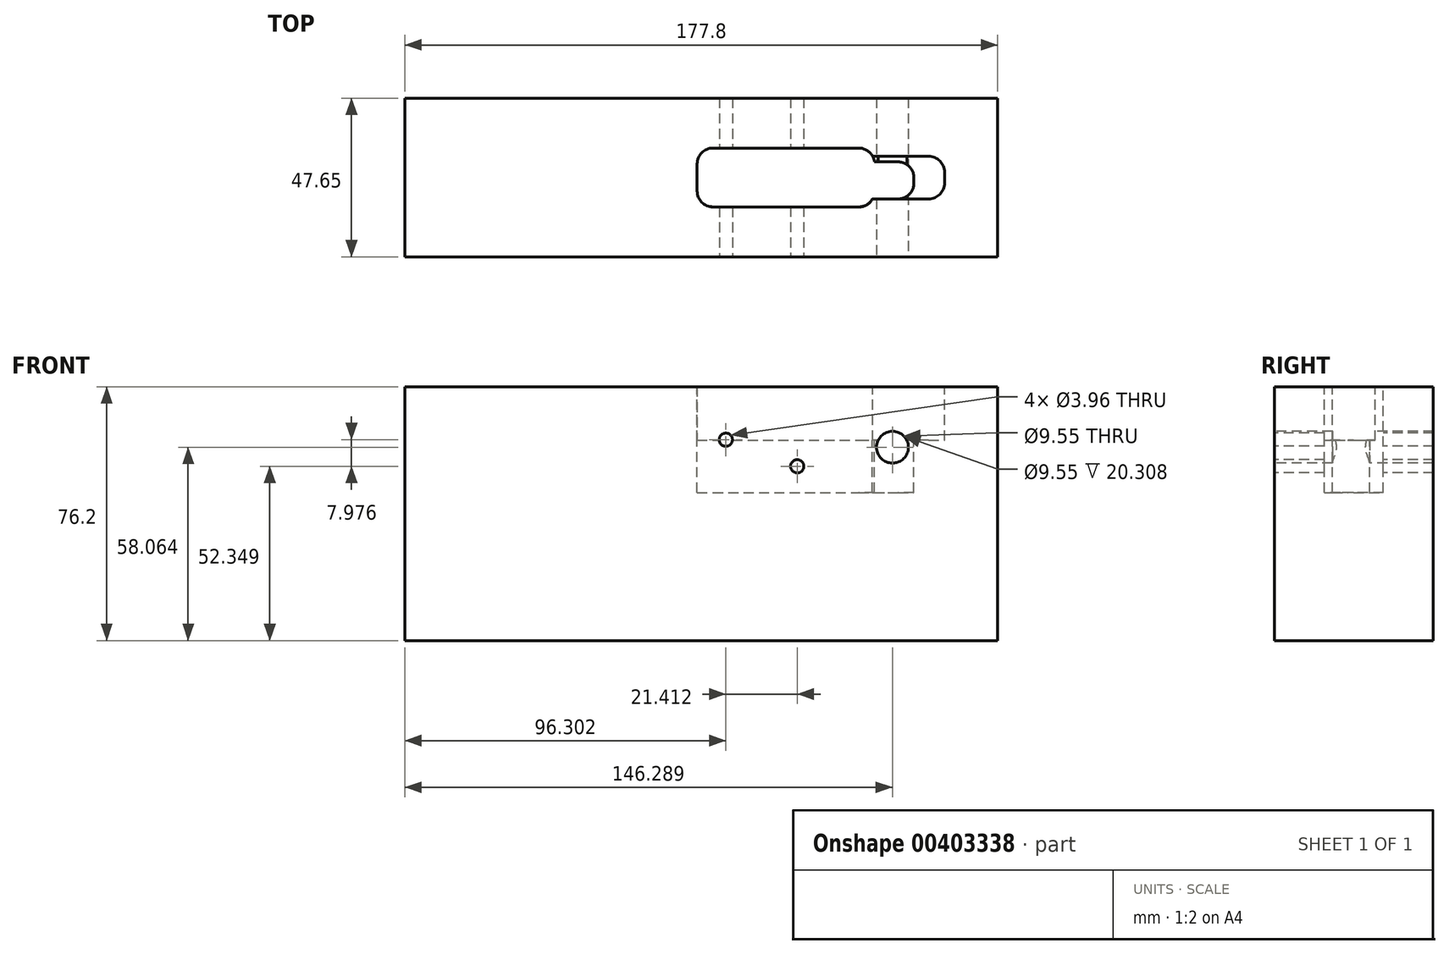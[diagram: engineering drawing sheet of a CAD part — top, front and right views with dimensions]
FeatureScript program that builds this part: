
annotation { "Feature Type Name" : "Feature", "Feature Type Description" : "" }
export const myFeature = defineFeature(function(context is Context, id is Id, definition is map)
    precondition{}
    {
        {
            var Q0;
            Q0=qCreatedBy(makeId("Top.planeOp"),FACE);
            var sketch = newSketch(context, id + "F0", { "sketchPlane" : qUnion([Q0])});
            skLineSegment(sketch, "E0.bottom", {"start": v(-4.76, 47.65) * mm, "end": v(173.04, 47.65) * mm});
            skLineSegment(sketch, "E0.top", {"start": v(-4.76, 0) * mm, "end": v(173.04, 0) * mm});
            skLineSegment(sketch, "E0.left", {"start": v(-4.76, 47.65) * mm, "end": v(-4.76, 0) * mm});
            skLineSegment(sketch, "E0.right", {"start": v(173.04, 47.65) * mm, "end": v(173.04, 0) * mm});
            skLineSegment(sketch, "E1", {"start": v(173, 23.83) * mm, "end": v(-20.73, 23.83) * mm, "construction": true});
            skPoint(sketch, "E1.startSnap0", {"position": v(173.04, 23.83) * mm});
            skPoint(sketch, "E1.endSnap0", {"position": v(-4.76, 23.83) * mm});
            skSolve(sketch);
        }
        {
            var Q0;
            Q0=makeQuery(id+"F0.imprint","IMPRINT",FACE,{"disambiguationData":[TD([[makeQuery(id+"F0.imprint","IMPRINT",EDGE,{"derivedFrom":sQuery(id+"F0.wireOp",EDGE,"E0.bottom")}),-1.0]])]});
            extrude(context, id + "F1", {"entities" : qUnion([Q0]), "oppositeDirection" : true, "depth" : 69.85 * mm, "hasSecondDirection" : true, "secondDirectionOppositeDirection" : false, "secondDirectionDepth" : 6.35 * mm});
        }
        {
            var Q0;
            Q0=qCreatedBy(makeId("Front.planeOp"),FACE);
            var sketch = newSketch(context, id + "F2", { "sketchPlane" : qUnion([Q0])});
            skCircle(sketch, "E2", {"center": v(0, 0) * mm, "radius": 3.18 * mm, "construction": true});
            skCircle(sketch, "E3", {"center": v(141.53, -11.79) * mm, "radius": 4.78 * mm});
            skCircle(sketch, "E4", {"center": v(112.95, -17.5) * mm, "radius": 1.98 * mm});
            skCircle(sketch, "E5", {"center": v(91.54, -9.52) * mm, "radius": 1.98 * mm});
            skCircle(sketch, "E6", {"center": v(161.93, 0) * mm, "radius": 3.18 * mm, "construction": true});
            skSolve(sketch);
        }
        {
            var Q0;
            Q0=qSketchRegion(id+"F2",true);
            extrude(context, id + "F3", {"entities" : qUnion([Q0]), "operationType" : NewBodyOperationType.REMOVE, "endBound" : BoundingType.THROUGH_ALL, "oppositeDirection" : true, "depth" : 25.4 * mm});
        }
        {
            var Q0;
            Q0=makeQuery(id+"F1.opExtrude","CAP_FACE",FACE,{"disambiguationData":[OSD([sQuery(id+"F0.wireOp",EDGE,"E0.bottom"),sQuery(id+"F0.wireOp",EDGE,"E0.top"),sQuery(id+"F0.wireOp",EDGE,"E0.left"),sQuery(id+"F0.wireOp",EDGE,"E0.right")])],"isStart":true});
            var sketch = newSketch(context, id + "F4", { "sketchPlane" : qUnion([Q0])});
            skLineSegment(sketch, "E7.right", {"start": v(148.53, 23.06) * mm, "end": v(148.5, 23.05) * mm});
            skPoint(sketch, "E8.visualSharp", {"position": v(135.54, 17.38) * mm});
            skLineSegment(sketch, "E9.bottom", {"start": v(87.7, 32.6) * mm, "end": v(131.4, 32.6) * mm});
            skLineSegment(sketch, "E9.top", {"start": v(87.7, 14.95) * mm, "end": v(131.4, 14.95) * mm});
            skLineSegment(sketch, "E9.left", {"start": v(82.93, 27.84) * mm, "end": v(82.93, 19.72) * mm});
            skArc(sketch, "E10.filletArc", {"start": v(87.7, 32.6) * mm, "mid": v(84.33, 31.21) * mm, "end": v(82.93, 27.84) * mm});
            skArc(sketch, "E11.filletArc", {"start": v(82.93, 19.72) * mm, "mid": v(84.33, 16.35) * mm, "end": v(87.7, 14.95) * mm});
            skLineSegment(sketch, "E12", {"start": v(53.04, 23.78) * mm, "end": v(165.2, 23.78) * mm, "construction": true});
            skLineSegment(sketch, "E13", {"start": v(135.54, 17.38) * mm, "end": v(152.4, 17.38) * mm});
            skLineSegment(sketch, "E14", {"start": v(157.16, 22.14) * mm, "end": v(157.16, 25.42) * mm});
            skLineSegment(sketch, "E15", {"start": v(152.4, 30.18) * mm, "end": v(135.54, 30.18) * mm});
            skPoint(sketch, "E16.visualSharp", {"position": v(157.16, 30.18) * mm});
            skArc(sketch, "E16.filletArc", {"start": v(157.16, 25.42) * mm, "mid": v(155.77, 28.79) * mm, "end": v(152.4, 30.18) * mm});
            skPoint(sketch, "E17.visualSharp", {"position": v(157.16, 17.38) * mm});
            skArc(sketch, "E17.filletArc", {"start": v(152.4, 17.38) * mm, "mid": v(155.77, 18.77) * mm, "end": v(157.16, 22.14) * mm});
            skArc(sketch, "E18.filletArc", {"start": v(135.55, 30.16) * mm, "mid": v(133.8, 31.95) * mm, "end": v(131.4, 32.6) * mm});
            skArc(sketch, "E19.filletArc", {"start": v(131.4, 14.95) * mm, "mid": v(133.8, 15.6) * mm, "end": v(135.55, 17.39) * mm});
            skSolve(sketch);
        }
        {
            var Q0;
            Q0=qSketchRegion(id+"F4",true);
            extrude(context, id + "F5", {"entities" : qUnion([Q0]), "operationType" : NewBodyOperationType.REMOVE, "oppositeDirection" : true, "depth" : 16.05 * mm});
        }
        {
            var Q0;
            {var subQ2=sQuery(id+"F4.wireOp",EDGE,"E9.bottom");Q0=makeQuery(id+"F4.imprint","IMPRINT",FACE,{"disambiguationData":[TD([[makeQuery(id+"F4.imprint","IMPRINT",EDGE,{"derivedFrom":subQ2}),1.0]])]});}
            var sketch = newSketch(context, id + "F6", { "sketchPlane" : qUnion([Q0])});
            skLineSegment(sketch, "E20.bottom", {"start": v(136.12, 28.5) * mm, "end": v(143.2, 28.5) * mm});
            skPoint(sketch, "E21.visualSharp", {"position": v(3571.03, 28.5) * mm});
            skArc(sketch, "E22.filletArc", {"start": v(111.07, 17.4) * mm, "mid": v(111.08, 17.4) * mm, "end": v(111.1, 17.4) * mm});
            skLineSegment(sketch, "E23.bottom", {"start": v(87.7, 32.65) * mm, "end": v(131.4, 32.65) * mm});
            skLineSegment(sketch, "E23.top", {"start": v(87.7, 15) * mm, "end": v(131.4, 15) * mm});
            skLineSegment(sketch, "E23.left", {"start": v(82.93, 27.89) * mm, "end": v(82.93, 19.76) * mm});
            skArc(sketch, "E24.filletArc", {"start": v(136.12, 28.5) * mm, "mid": v(134.54, 31.47) * mm, "end": v(131.4, 32.65) * mm});
            skArc(sketch, "E25.filletArc", {"start": v(131.4, 15) * mm, "mid": v(133.78, 15.64) * mm, "end": v(135.52, 17.38) * mm});
            skArc(sketch, "E26.filletArc", {"start": v(87.7, 32.65) * mm, "mid": v(84.33, 31.26) * mm, "end": v(82.93, 27.89) * mm});
            skArc(sketch, "E27.filletArc", {"start": v(82.93, 19.76) * mm, "mid": v(84.33, 16.4) * mm, "end": v(87.7, 15) * mm});
            skLineSegment(sketch, "E28", {"start": v(23.77, 23.83) * mm, "end": v(135.92, 23.83) * mm, "construction": true});
            skLineSegment(sketch, "E29", {"start": v(131.4, 53.22) * mm, "end": v(131.4, 32.65) * mm, "construction": true});
            skLineSegment(sketch, "E30", {"start": v(135.52, 17.38) * mm, "end": v(143.2, 17.38) * mm});
            skLineSegment(sketch, "E31", {"start": v(147.95, 23.75) * mm, "end": v(147.96, 22.15) * mm});
            skPoint(sketch, "E32.visualSharp", {"position": v(147.94, 28.5) * mm});
            skArc(sketch, "E32.filletArc", {"start": v(147.95, 23.75) * mm, "mid": v(146.55, 27.11) * mm, "end": v(143.2, 28.5) * mm});
            skPoint(sketch, "E33.visualSharp", {"position": v(147.97, 17.38) * mm});
            skArc(sketch, "E33.filletArc", {"start": v(143.2, 17.38) * mm, "mid": v(146.57, 18.78) * mm, "end": v(147.96, 22.15) * mm});
            skSolve(sketch);
        }
        {
            var Q0;
            Q0 = qSketchRegion(id + "F6", true);
            extrude(context, id + "F7", {"entities" : qUnion([Q0]), "operationType" : NewBodyOperationType.REMOVE, "oppositeDirection" : true, "offsetDistance" : 25.4 * mm, "depth" : 31.72 * mm});
        }
    });
